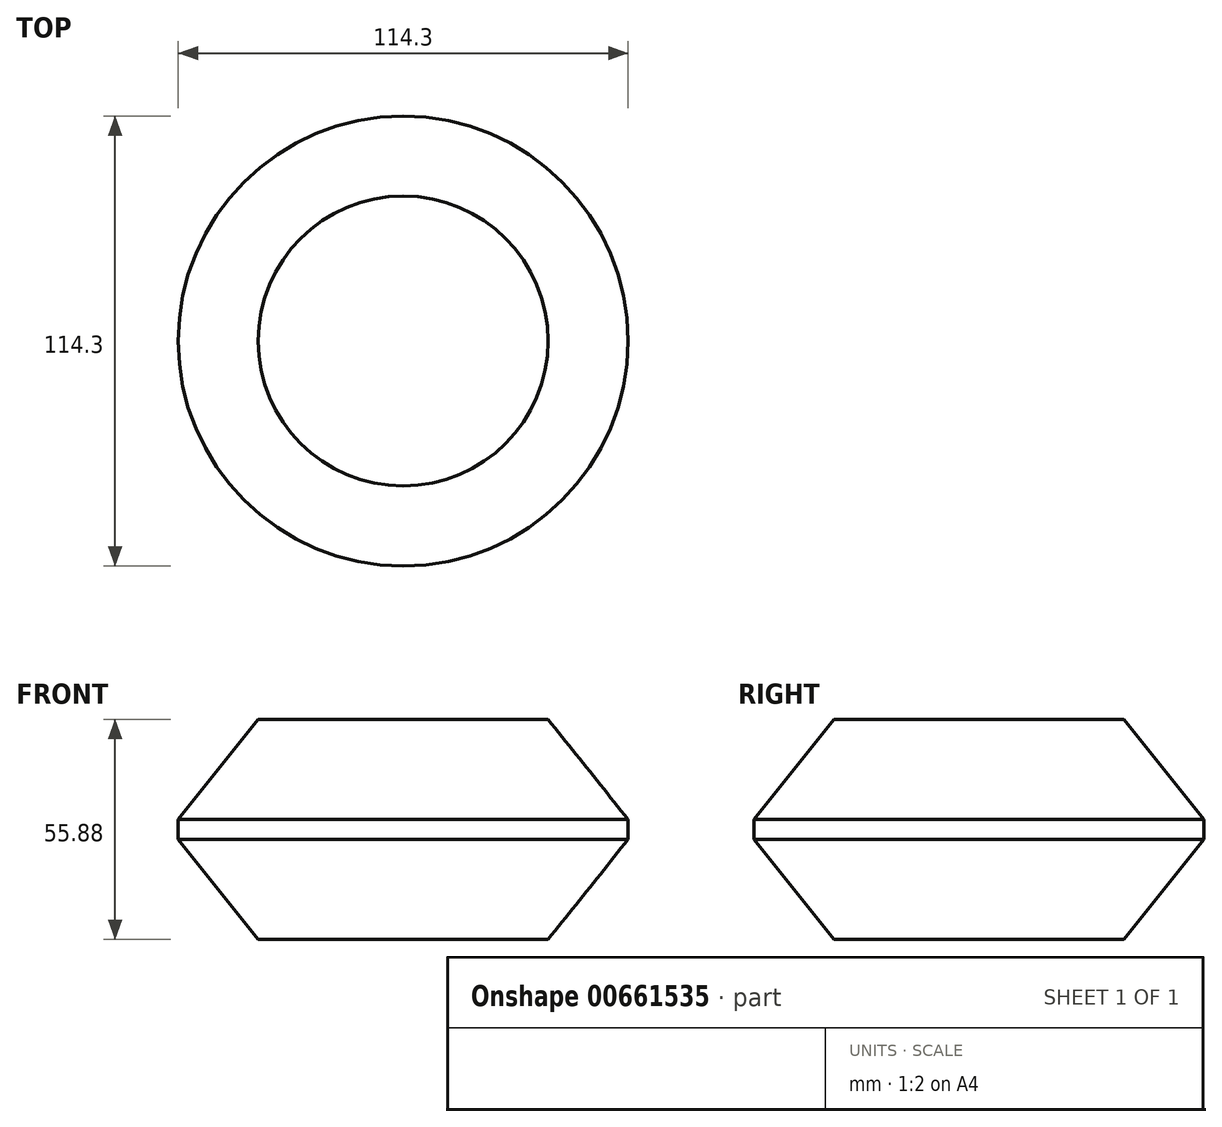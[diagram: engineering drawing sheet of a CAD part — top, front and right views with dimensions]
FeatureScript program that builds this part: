
annotation { "Feature Type Name" : "Feature", "Feature Type Description" : "" }
export const myFeature = defineFeature(function(context is Context, id is Id, definition is map)
    precondition{}
    {
        {
            var Q0;
            Q0=qCreatedBy(makeId("Top.planeOp"),FACE);
            var sketch = newSketch(context, id + "F0", { "sketchPlane" : qUnion([Q0])});
            skCircle(sketch, "E0", {"center": v(0, 0) * mm, "radius": 57.15 * mm});
            skSolve(sketch);
        }
        {
            var Q0;
            Q0=makeQuery(id+"F0.imprint","IMPRINT",FACE,{"disambiguationData":[TD([[makeQuery(id+"F0.imprint","IMPRINT",EDGE,{"derivedFrom":sQuery(id+"F0.wireOp",EDGE,"E0")}),1.0]])]});
            extrude(context, id + "F1", {"entities" : qUnion([Q0]), "depth" : 2.54 * mm, "offsetDistance" : 25.4 * mm});
        }
        {
            var Q0;
            Q0=makeQuery(id+"F1.opExtrude","CAP_FACE",FACE,{"disambiguationData":[OSD([sQuery(id+"F0.wireOp",EDGE,"E0")])],"isStart":false});
            cPlane(context, id + "F2", {"entities" : qUnion([Q0]), "cplaneType" : CPlaneType.OFFSET, "offset" : 25.4 * mm, "width" : 152.4 * mm, "height" : 152.4 * mm});
        }
        {
            var Q0;
            Q0=qCreatedBy(id+"F2.planeOp",FACE);
            var sketch = newSketch(context, id + "F3", { "sketchPlane" : qUnion([Q0])});
            skCircle(sketch, "E1", {"center": v(0, 0) * mm, "radius": 36.83 * mm});
            skSolve(sketch);
        }
        {
            var Q1;
            Q1=makeQuery(id+"F3.imprint","IMPRINT",FACE,{"disambiguationData":[TD([[makeQuery(id+"F3.imprint","IMPRINT",EDGE,{"derivedFrom":sQuery(id+"F3.wireOp",EDGE,"E1")}),1.0]])]});
            var Q2;
            Q2=makeQuery(id+"F1.opExtrude","CAP_FACE",FACE,{"disambiguationData":[OSD([sQuery(id+"F0.wireOp",EDGE,"E0")])],"isStart":false});
            loft(context, id + "F4", {"operationType" : NewBodyOperationType.ADD, "sheetProfilesArray" : [{ "sheetProfileEntities" : qUnion([Q1]) }, { "sheetProfileEntities" : qUnion([Q2]) }]});
        }
        {
            var Q0;
            Q0=makeQuery(id+"F1.opExtrude","SWEPT_BODY",BODY,{"disambiguationData":[OSD([sQuery(id+"F0.wireOp",EDGE,"E0")])]});
            var Q1;
            Q1=makeQuery(id+"F1.opExtrude","CAP_FACE",FACE,{"disambiguationData":[OSD([sQuery(id+"F0.wireOp",EDGE,"E0")])],"isStart":true});
            mirror(context, id + "F5", {"operationType" : NewBodyOperationType.ADD, "entities" : qUnion([Q0]), "mirrorPlane" : qUnion([Q1])});
        }
        {
            var Q0;
            Q0=qCreatedBy(makeId("Top.planeOp"),FACE);
            var sketch = newSketch(context, id + "F6", { "sketchPlane" : qUnion([Q0])});
            skArc(sketch, "E2", {"start": v(16.33, 55.77) * mm, "mid": v(0, 95.9) * mm, "end": v(-14.75, 55.16) * mm});
            skSolve(sketch);
        }
        {
            var Q0;
            Q0=sQuery(id+"F6.wireOp",EDGE,"E2");
            extrude(context, id + "F7", {"bodyType" : ToolBodyType.SURFACE, "surfaceEntities" : qUnion([Q0]), "depth" : 7.62 * mm, "offsetDistance" : 25.4 * mm});
        }
    });
